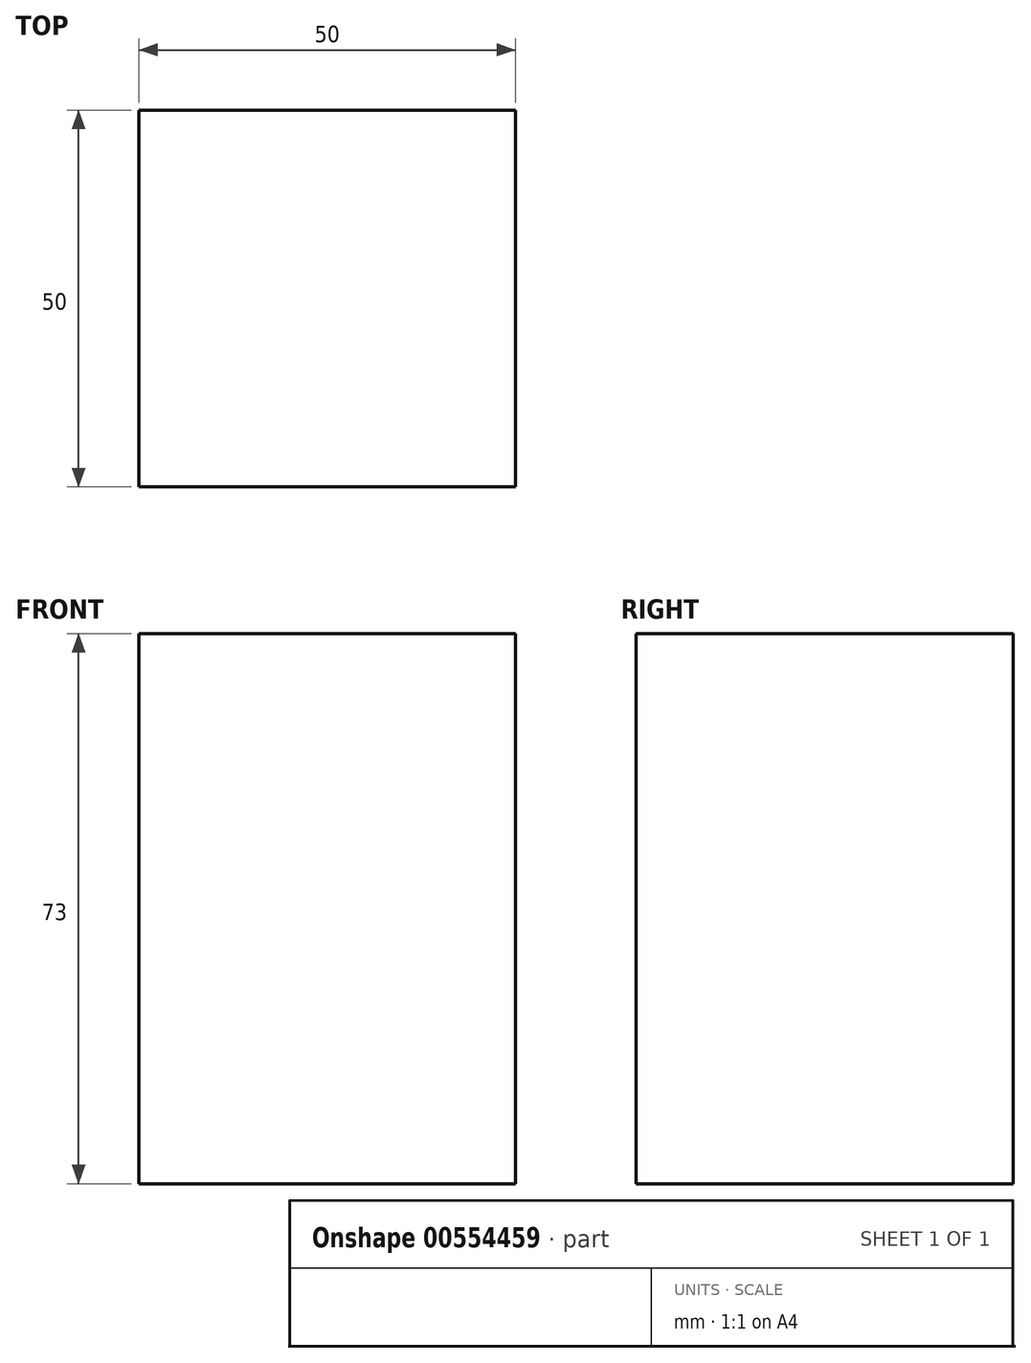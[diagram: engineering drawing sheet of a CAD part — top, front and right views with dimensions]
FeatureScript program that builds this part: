
annotation { "Feature Type Name" : "Feature", "Feature Type Description" : "" }
export const myFeature = defineFeature(function(context is Context, id is Id, definition is map)
    precondition{}
    {
        {
            var Q0;
            Q0=qCreatedBy(makeId("Top.planeOp"),FACE);
            var sketch = newSketch(context, id + "F0", { "sketchPlane" : qUnion([Q0])});
            skLineSegment(sketch, "E0.bottom", {"start": v(-18.94, -18.46) * mm, "end": v(31.06, -18.46) * mm});
            skLineSegment(sketch, "E0.top", {"start": v(-18.94, 31.54) * mm, "end": v(31.06, 31.54) * mm});
            skLineSegment(sketch, "E0.left", {"start": v(-18.94, -18.46) * mm, "end": v(-18.94, 31.54) * mm});
            skLineSegment(sketch, "E0.right", {"start": v(31.06, -18.46) * mm, "end": v(31.06, 31.54) * mm});
            skSolve(sketch);
        }
        {
            var Q0;
            Q0 = qSketchRegion(id + "F0", true);
            extrude(context, id + "F1", {"entities" : qUnion([Q0]), "depth" : 25 * mm, "offsetDistance" : 25 * mm});
        }
        {
            var Q0;
            Q0=makeQuery(id+"F1.opExtrude","CAP_FACE",FACE,{"disambiguationData":[OSD([sQuery(id+"F0.wireOp",EDGE,"E0.bottom"),sQuery(id+"F0.wireOp",EDGE,"E0.top"),sQuery(id+"F0.wireOp",EDGE,"E0.left"),sQuery(id+"F0.wireOp",EDGE,"E0.right")])],"isStart":false});
            extrude(context, id + "F2", {"entities" : qUnion([Q0]), "operationType" : NewBodyOperationType.ADD, "depth" : 48 * mm, "offsetDistance" : 25 * mm});
        }
    });
